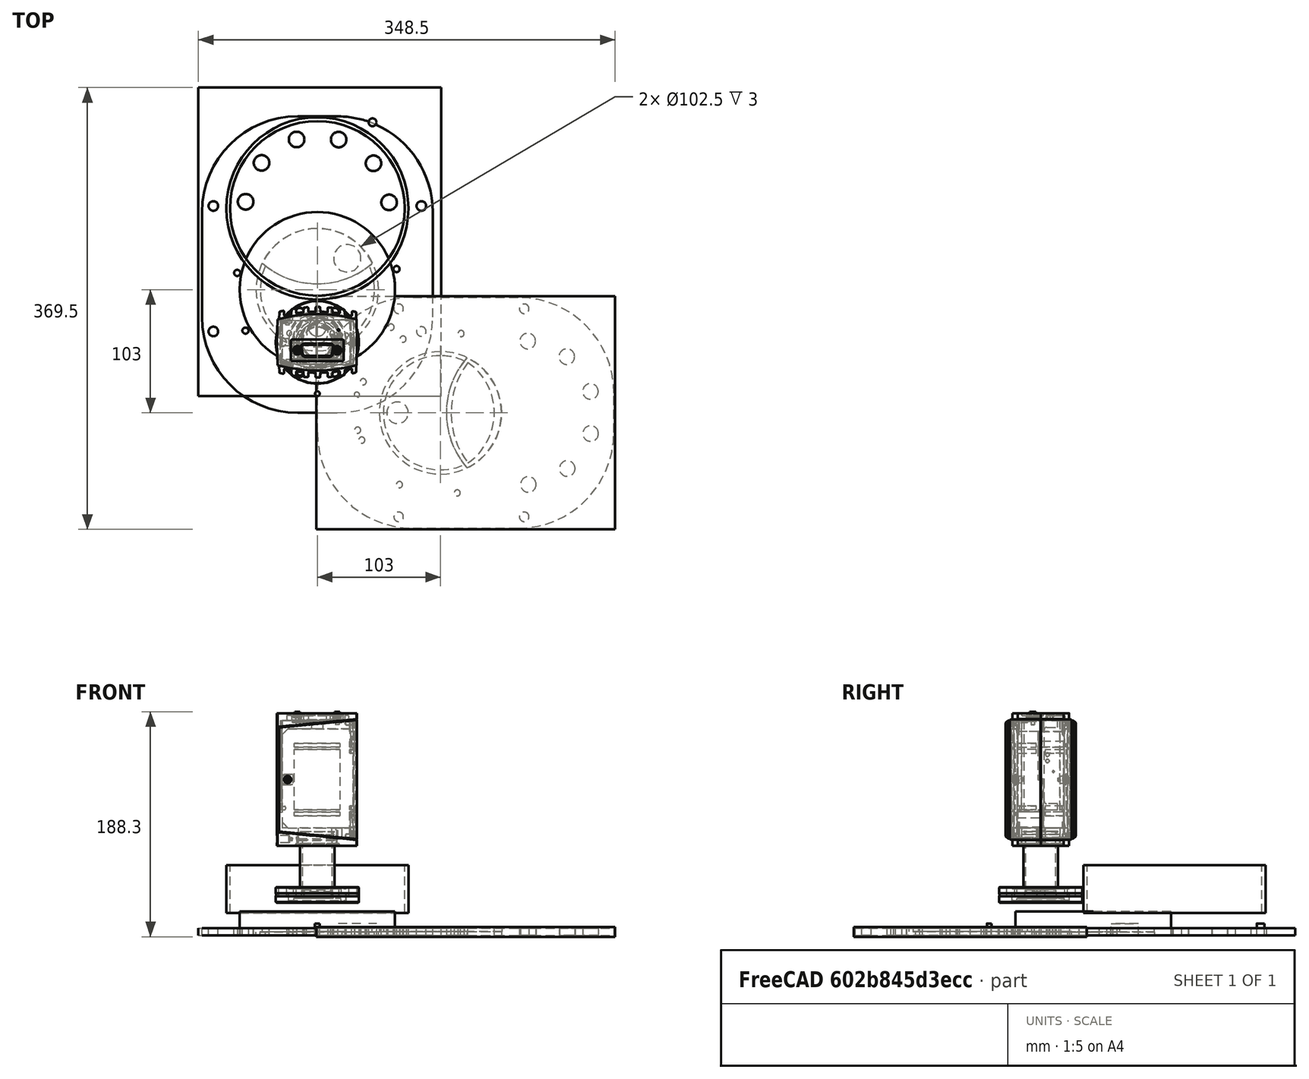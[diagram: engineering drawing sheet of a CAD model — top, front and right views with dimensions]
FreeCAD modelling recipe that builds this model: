
FCSTD DOCUMENT  (FreeCAD 0.18R16033 (Git))
Label: mk_3_5
License: All rights reserved
LicenseURL: http://en.wikipedia.org/wiki/All_rights_reserved
objects: Part::Cylinder×38, Part::FeaturePython×8, Path::FeaturePython×8, Part::Cut×7, Part::MultiFuse×6, Part::MultiCommon×4, Part::Box×3, Part::Fillet×2, App::FeaturePython×2, App::DocumentObjectGroup×2, Path::FeatureCompoundPython×2, Spreadsheet::Sheet×1, Part::Feature×1
note: 72 computed .brp shape members not serialized (recipe doc carries the construction recipe); baked Part::Feature solids carry a one-line shape summary decoded from their .brp

FEATURE [Part::Box] Box  label="Cube"
  AttacherType = Attacher::AttachEngine3D
  Height = 6.2
  Length = 193
  Placement = pos=(-96.5,0,0) rot=(0,0,1;0rad)
  Width = 248
FEATURE [Part::Cylinder] Cylinder004  label="Chamber001"
  Angle = 360
  AttacherType = Attacher::AttachEngine3D
  Height = 20
  Placement = pos=(0,149,0) rot=(0,0,1;0rad)
  Radius = 70.0875
  expr: Placement.Base.x = 0
  expr: Radius = 5.5625 * 25.2 / 2
FEATURE [Part::Cylinder] Cylinder005
  Angle = 360
  AttacherType = Attacher::AttachEngine3D
  Height = 20
  Placement = pos=(0,74,0) rot=(0,0,1;0rad)
  Radius = 51
  expr: Placement.Base.x = 0
  expr: Radius = 102 / 2
FEATURE [Part::MultiCommon] Common  label="Inlet"
  Placement = pos=(0,29,0) rot=(0,0,1;0rad)
  Shapes = -> [Cylinder004,Cylinder005]
FEATURE [Part::Cylinder] Cylinder012  label="Threaded"
  Angle = 360
  AttacherType = Attacher::AttachEngine3D
  Height = 19.5
  Placement = pos=(36.025,58.5,-4) rot=(0,0,1;0rad)
  Radius = 2.57969
  expr: Placement.Base.x = 105 - 68.675 - 0.3
  expr: Radius = 13 / 64 * 25.4 / 2
FEATURE [Part::FeaturePython] Array  label="TurboMounts"  # Draft array (typed FeaturePython)
  Angle = 208
  ArrayType = 1
  Axis = (0,0,1)
  Base = -> Cylinder012
  Center = (0,0,0)
  Fuse = false
  IntervalAxis = (0,0,0)
  IntervalX = (1,0,0)
  IntervalY = (0,1,0)
  IntervalZ = (0,0,0)
  NumberPolar = 6
  NumberX = 2
  NumberY = 2
  NumberZ = 1
  Placement = pos=(0,102,0) rot=(0,0,1;1.90241rad)
FEATURE [Part::Cylinder] Cylinder051  label="Flange001"
  Angle = 360
  AttacherType = Attacher::AttachEngine3D
  Height = 3
  Placement = pos=(0,68,0) rot=(0,0,1;0rad)
  Radius = 51.25
  expr: Radius = 102.5 / 2
FEATURE [Part::Cylinder] Cylinder052  label="Flange002"
  Angle = 360
  AttacherType = Attacher::AttachEngine3D
  Height = 3
  Placement = pos=(0,68,0) rot=(0,0,1;0rad)
  Radius = 47.75
  expr: Radius = 51.25 - 3.5
FEATURE [Part::Cut] Cut001  label="CenteringRingGroove"
  Base = -> Cylinder051
  Placement = pos=(0,35,0) rot=(0,0,1;0rad)
  Tool = -> Cylinder052
FEATURE [Part::Cylinder] Cylinder002  label="ChamberWall"
  Angle = 360
  AttacherType = Attacher::AttachEngine3D
  Height = 40
  Placement = pos=(0,148,0) rot=(0,0,1;0rad)
  Radius = 76.2
  expr: Radius = 3 * 25.4
FEATURE [Part::Cylinder] Cylinder008  label="ChamberWall001"
  Angle = 360
  AttacherType = Attacher::AttachEngine3D
  Height = 40
  Placement = pos=(0,148,0) rot=(0,0,1;0rad)
  Radius = 73.025
  expr: Radius = (3 - 0.125) * 25.4
FEATURE [Part::Cut] Cut  label="ChamberWall002"
  Base = -> Cylinder002
  Placement = pos=(0,23,19) rot=(0,0,1;0rad)
  Tool = -> Cylinder008
FEATURE [Spreadsheet::Sheet] Spreadsheet  label="Sizes"
  cells = A1=Baseplate width; B1(BASE_WIDTH)=195; A2=Baseplate length; B2(BASE_LENGTH)=255
FEATURE [Part::Cylinder] Cylinder
  Angle = 360
  AttacherType = Attacher::AttachEngine3D
  Height = 10
  Placement = pos=(25,129.26,0) rot=(0,0,1;0rad)
  Radius = 11.4
  expr: Placement.Base.y = 117.86 + 11.4
  expr: Radius = 22.8 / 2
FEATURE [Part::Cylinder] Cylinder053  label="Flange"
  Angle = 360
  AttacherType = Attacher::AttachEngine3D
  Height = 20
  Placement = pos=(0,103,0) rot=(0,0,1;0rad)
  Radius = 65
  expr: Placement.Base.x = 0
  expr: Radius = 130 / 2
FEATURE [Part::Cylinder] Cylinder054  label="Cylinder006"
  Angle = 360
  AttacherType = Attacher::AttachEngine3D
  Height = 10
  Placement = pos=(46.19,243,0) rot=(0,0,1;0rad)
  Radius = 3.275
  expr: Radius = 6.55 / 2
FEATURE [Part::Feature] Part__Feature002  label="353-502"
  Placement = pos=(0,59,75) rot=(1,0,0;1.5708rad)
  shape: bbox 69.52 x 69.52 x 159.7 mm, 770 faces, 3 solids (baked)
FEATURE [Part::Cylinder] Cylinder157  label="Gland1"
  Angle = 360
  AttacherType = Attacher::AttachEngine3D
  Height = 3.175
  Radius = 24
FEATURE [Part::Cylinder] Cylinder158  label="Cylinder010"
  Angle = 360
  AttacherType = Attacher::AttachEngine3D
  Height = 41.275
  Radius = 20.635
  expr: Radius = (25.4 + 15.87) / 2
  expr: Height = 25.4 + 15.875
FEATURE [Part::Cut] Cut020
  Base = -> Cylinder157
  Placement = pos=(0,61,0) rot=(0,0,1;0rad)
  Tool = -> Cylinder158
FEATURE [Part::Cylinder] Cylinder159  label="Cylinder011"
  Angle = 360
  AttacherType = Attacher::AttachEngine3D
  Height = 21
  Placement = pos=(0,67,-4) rot=(0,0,1;0rad)
  Radius = 9
  expr: Placement.Base.x = 0
FEATURE [Part::Cylinder] Cylinder163  label="Cylinder015"
  Angle = 360
  AttacherType = Attacher::AttachEngine3D
  Height = 29
  Placement = pos=(-14.5,33.7,-7) rot=(0,0,1;0rad)
  Radius = 2.58
FEATURE [Part::Cylinder] Cylinder164  label="Cylinder016"
  Angle = 360
  AttacherType = Attacher::AttachEngine3D
  Height = 29
  Placement = pos=(15,33,-9) rot=(0,0,1;0rad)
  Radius = 2.28
FEATURE [Part::Cylinder] Cylinder165  label="Cylinder017"
  Angle = 360
  AttacherType = Attacher::AttachEngine3D
  Height = 10
  Placement = pos=(-87,173,0) rot=(0,0,1;0rad)
  Radius = 4
  expr: Radius = 4
FEATURE [Part::Cylinder] Cylinder166  label="Cylinder018"
  Angle = 360
  AttacherType = Attacher::AttachEngine3D
  Height = 10
  Placement = pos=(87,68,0) rot=(0,0,1;0rad)
  Radius = 4
  expr: Radius = 4
FEATURE [Part::Cylinder] Cylinder167  label="Cylinder019"
  Angle = 360
  AttacherType = Attacher::AttachEngine3D
  Height = 10
  Placement = pos=(-87,68,0) rot=(0,0,1;0rad)
  Radius = 4
  expr: Radius = 4
FEATURE [Part::Cylinder] Cylinder168  label="Cylinder020"
  Angle = 360
  AttacherType = Attacher::AttachEngine3D
  Height = 10
  Placement = pos=(87,173,0) rot=(0,0,1;0rad)
  Radius = 4
  expr: Radius = 4
FEATURE [Part::Box] Box001  label="Cube001"
  AttacherType = Attacher::AttachEngine3D
  Height = 6.2
  Length = 203
  Placement = pos=(-99.5,14,0) rot=(0,0,1;0rad)
  Width = 258
FEATURE [Part::Cylinder] Cylinder169  label="Cylinder021"
  Angle = 360
  AttacherType = Attacher::AttachEngine3D
  Height = 10
  Placement = pos=(0,16,0) rot=(0,0,1;0rad)
  Radius = 2
FEATURE [Part::Cylinder] Cylinder170  label="Cylinder022"
  Angle = 360
  AttacherType = Attacher::AttachEngine3D
  Height = 10
  Placement = pos=(60,181,0) rot=(0,0,1;0rad)
  Radius = 6.5
  expr: Radius = 13 / 2
FEATURE [Part::FeaturePython] Array001  # Draft array (typed FeaturePython)
  Angle = 170
  ArrayType = 1
  Axis = (0,0,1)
  Base = -> Cylinder170
  Center = (0,176,0)
  Fuse = false
  IntervalAxis = (0,0,0)
  IntervalX = (1,0,0)
  IntervalY = (0,1,0)
  IntervalZ = (0,0,0)
  NumberPolar = 6
  NumberX = 2
  NumberY = 2
  NumberZ = 1
  Placement = pos=(0,-5,0) rot=(0,0,1;0rad)
  expr: Center.y = 148 + 28
FEATURE [Part::Fillet] Fillet
  Base = -> Box
  Edges = 4 edges r=80: [Edge1,Edge3,Edge5,Edge7]
FEATURE [Part::MultiFuse] Fusion
  Shapes = -> [Common,Array,Cut001,Cylinder164,Cylinder163,Cylinder159,Cylinder165,Cylinder166,Cylinder167,Cylinder168]
FEATURE [Part::MultiFuse] Fusion001
  Shapes = -> [Fusion,Array001]
FEATURE [Part::Cut] Cut021
  Base = -> Fillet
  Tool = -> Fusion001
FEATURE [Part::Cut] Cut022
  Base = -> Fillet
  Placement = pos=(0,0,6.2) rot=(0,1,0;3.14159rad)
  Tool = -> Fusion001
FEATURE [Part::Cylinder] Cylinder171
  Angle = 360
  AttacherType = Attacher::AttachEngine3D
  Height = 20
  Placement = pos=(0,68,0) rot=(0,0,1;0rad)
  Radius = 51
  expr: Placement.Base.x = 0
  expr: Radius = 102 / 2
FEATURE [Part::Cylinder] Cylinder172  label="Chamber002"
  Angle = 360
  AttacherType = Attacher::AttachEngine3D
  Height = 6.2
  Placement = pos=(0,153,0) rot=(0,0,1;0rad)
  Radius = 70.0875
  expr: Placement.Base.x = 0
  expr: Radius = 5.5625 * 25.2 / 2
FEATURE [Part::MultiCommon] Common001  label="Inlet001"
  Placement = pos=(0,29,0) rot=(0,0,1;0rad)
  Shapes = -> [Cylinder172,Cylinder171]
FEATURE [Part::MultiFuse] Fusion002
  Placement = pos=(0,0,0) rot=(0,0,-1;1.5708rad)
  Shapes = -> [Common001,Cut022]
FEATURE [Part::Cylinder] Cylinder173  label="Chamber003"
  Angle = 360
  AttacherType = Attacher::AttachEngine3D
  Height = 6.2
  Placement = pos=(0,159,0) rot=(0,0,1;0rad)
  Radius = 70.0875
  expr: Placement.Base.x = 0
  expr: Radius = 5.5625 * 25.2 / 2
FEATURE [Part::Cylinder] Cylinder174
  Angle = 360
  AttacherType = Attacher::AttachEngine3D
  Height = 20
  Placement = pos=(0,63,0) rot=(0,0,1;0rad)
  Radius = 51
  expr: Placement.Base.x = 0
  expr: Radius = 102 / 2
FEATURE [Part::Cylinder] Cylinder175
  Angle = 360
  AttacherType = Attacher::AttachEngine3D
  Height = 10
  Placement = pos=(87,173,0) rot=(0,0,1;0rad)
  Radius = 4
  expr: Radius = 4
FEATURE [Part::Cylinder] Cylinder176  label="Chamber004"
  Angle = 360
  AttacherType = Attacher::AttachEngine3D
  Height = 20
  Placement = pos=(0,149,0) rot=(0,0,1;0rad)
  Radius = 70.0875
  expr: Placement.Base.x = 0
  expr: Radius = 5.5625 * 25.2 / 2
FEATURE [Part::Cylinder] Cylinder177  label="Cylinder176"
  Angle = 360
  AttacherType = Attacher::AttachEngine3D
  Height = 29
  Placement = pos=(15,33,-9) rot=(0,0,1;0rad)
  Radius = 2.28
FEATURE [Part::Cylinder] Cylinder178  label="Threaded001"
  Angle = 360
  AttacherType = Attacher::AttachEngine3D
  Height = 19.5
  Placement = pos=(36.025,58.5,-4) rot=(0,0,1;0rad)
  Radius = 2.57969
  expr: Placement.Base.x = 105 - 68.675 - 0.3
  expr: Radius = 13 / 64 * 25.4 / 2
FEATURE [Part::FeaturePython] Array002  label="TurboMounts001"  # Draft array (typed FeaturePython)
  Angle = 208
  ArrayType = 1
  Axis = (0,0,1)
  Base = -> Cylinder178
  Center = (0,0,0)
  Fuse = false
  IntervalAxis = (0,0,0)
  IntervalX = (1,0,0)
  IntervalY = (0,1,0)
  IntervalZ = (0,0,0)
  NumberPolar = 6
  NumberX = 2
  NumberY = 2
  NumberZ = 1
  Placement = pos=(0,102,0) rot=(0,0,1;1.90241rad)
FEATURE [Part::Cylinder] Cylinder179  label="Flange003"
  Angle = 360
  AttacherType = Attacher::AttachEngine3D
  Height = 3
  Placement = pos=(0,68,0) rot=(0,0,1;0rad)
  Radius = 51.25
  expr: Radius = 102.5 / 2
FEATURE [Part::Cylinder] Cylinder180  label="Cylinder177"
  Angle = 360
  AttacherType = Attacher::AttachEngine3D
  Height = 10
  Placement = pos=(60,181,0) rot=(0,0,1;0rad)
  Radius = 6.5
  expr: Radius = 13 / 2
FEATURE [Part::Cylinder] Cylinder181  label="Cylinder178"
  Angle = 360
  AttacherType = Attacher::AttachEngine3D
  Height = 29
  Placement = pos=(-14.5,33.7,-7) rot=(0,0,1;0rad)
  Radius = 2.58
FEATURE [Part::Cylinder] Cylinder182  label="Cylinder179"
  Angle = 360
  AttacherType = Attacher::AttachEngine3D
  Height = 10
  Placement = pos=(-87,173,0) rot=(0,0,1;0rad)
  Radius = 4
  expr: Radius = 4
FEATURE [Part::Cylinder] Cylinder183  label="Cylinder180"
  Angle = 360
  AttacherType = Attacher::AttachEngine3D
  Height = 21
  Placement = pos=(0,67,-4) rot=(0,0,1;0rad)
  Radius = 9
  expr: Placement.Base.x = 0
FEATURE [Part::Cylinder] Cylinder184  label="Cylinder181"
  Angle = 360
  AttacherType = Attacher::AttachEngine3D
  Height = 10
  Placement = pos=(87,68,0) rot=(0,0,1;0rad)
  Radius = 4
  expr: Radius = 4
FEATURE [Part::Cylinder] Cylinder185  label="Flange004"
  Angle = 360
  AttacherType = Attacher::AttachEngine3D
  Height = 3
  Placement = pos=(0,68,0) rot=(0,0,1;0rad)
  Radius = 47.75
  expr: Radius = 51.25 - 3.5
FEATURE [Part::Cut] Cut023  label="CenteringRingGroove001"
  Base = -> Cylinder179
  Placement = pos=(0,35,0) rot=(0,0,1;0rad)
  Tool = -> Cylinder185
FEATURE [Part::FeaturePython] Array003  # Draft array (typed FeaturePython)
  Angle = 170
  ArrayType = 1
  Axis = (0,0,1)
  Base = -> Cylinder180
  Center = (0,176,0)
  Fuse = false
  IntervalAxis = (0,0,0)
  IntervalX = (1,0,0)
  IntervalY = (0,1,0)
  IntervalZ = (0,0,0)
  NumberPolar = 6
  NumberX = 2
  NumberY = 2
  NumberZ = 1
  Placement = pos=(0,-5,0) rot=(0,0,1;0rad)
  expr: Center.y = 148 + 28
FEATURE [Part::Cylinder] Cylinder186
  Angle = 360
  AttacherType = Attacher::AttachEngine3D
  Height = 20
  Placement = pos=(0,74,0) rot=(0,0,1;0rad)
  Radius = 51
  expr: Placement.Base.x = 0
  expr: Radius = 102 / 2
FEATURE [Part::MultiCommon] Common002  label="Inlet002"
  Placement = pos=(0,29,0) rot=(0,0,1;0rad)
  Shapes = -> [Cylinder176,Cylinder186]
FEATURE [Part::Cylinder] Cylinder187
  Angle = 360
  AttacherType = Attacher::AttachEngine3D
  Height = 10
  Placement = pos=(-87,68,0) rot=(0,0,1;0rad)
  Radius = 4
  expr: Radius = 4
FEATURE [Part::MultiFuse] Fusion005
  Shapes = -> [Common002,Array002,Cut023,Cylinder177,Cylinder181,Cylinder183,Cylinder182,Cylinder184,Cylinder187,Cylinder175]
FEATURE [Part::MultiFuse] Fusion004
  Shapes = -> [Fusion005,Array003]
FEATURE [Part::Box] Box002  label="Cube002"
  AttacherType = Attacher::AttachEngine3D
  Height = 6.2
  Length = 193
  Placement = pos=(-96.5,0,0) rot=(0,0,1;0rad)
  Width = 248
FEATURE [Part::Fillet] Fillet001
  Base = -> Box002
  Edges = 4 edges r=80: [Edge1,Edge3,Edge5,Edge7]
FEATURE [Part::MultiCommon] Common003  label="Inlet003"
  Placement = pos=(0,29,0) rot=(0,0,1;0rad)
  Shapes = -> [Cylinder173,Cylinder174]
FEATURE [Part::Cut] Cut024
  Base = -> Fillet001
  Placement = pos=(0,0,6.2) rot=(0,1,0;3.14159rad)
  Tool = -> Fusion004
FEATURE [Part::MultiFuse] Fusion003
  Placement = pos=(0,0,0) rot=(0,0,-1;1.5708rad)
  Shapes = -> [Common003,Cut024]
FEATURE [App::FeaturePython] SetupSheet  # Path/CAM operation (typed FeaturePython)
  ClearanceHeightExpression = OpStockZMax+SetupSheet.ClearanceHeightOffset
  ClearanceHeightOffset = 5
  FinalDepthExpression = OpFinalDepth
  HorizRapid = 0
  SafeHeightExpression = OpStockZMax+SetupSheet.SafeHeightOffset
  SafeHeightOffset = 3
  StartDepthExpression = OpStartDepth
  StepDownExpression = OpToolDiameter
  VertRapid = 0
FEATURE [Part::FeaturePython] Clone  label="Model-Fusion003"  # Draft clone (typed FeaturePython)
  AttacherType = Attacher::AttachEngine3D
  Fuse = false
  Objects = -> [Fusion003]
  PathResource = Model
  Placement = pos=(0,0,0) rot=(0,0,-1;1.5708rad)
  Scale = (1,1,1)
FEATURE [App::DocumentObjectGroup] Model
  Group = -> [Clone]
FEATURE [Part::FeaturePython] Stock001  # WARN: FeaturePython — macro-defined, semantics opaque (R4)
  Base = -> Model
  ExtXneg = 1
  ExtXpos = 1
  ExtYneg = 1
  ExtYpos = 1
  ExtZneg = 1
  ExtZpos = 1
  Placement = pos=(-1.77e-14,-96.5,-9e-16) rot=(0,0,1;0rad)
  StockType = FromBase
FEATURE [Path::FeaturePython] T2__250_End_Mill  label="T2: 250 End Mill"  # Path/CAM operation (typed FeaturePython)
  HorizFeed = 11
  HorizRapid = 0
  SpindleDir = 0
  SpindleSpeed = 13000
  ToolNumber = 1
  VertFeed = 1
  VertRapid = 0
  expr: HorizRapid = SetupSheet.HorizRapid
  expr: VertRapid = SetupSheet.VertRapid
FEATURE [Path::FeaturePython] Contour  # Path/CAM operation (typed FeaturePython)
  Active = false
  AreaParams:
    OpenMode = 0
    Angle = 45.0
    MinArcPoints = 4
    Coplanar = 2
    Tolerance = 1e-07
    CleanDistance = 0.0
    PocketExtraOffset = 0.0
    RoundPrecision = 0.0
    AngleShift = 0.0
    SubjectFill = 0
    PocketMode = 0
    PocketLastStepover = 0.0
    Simplify = False
    SectionTolerance = 1e-06
    MaxArcPoints = 100
    Offset = 3.175
    Accuracy = 0.01
    LastStepover = 0.0
    PocketStepover = 0.0
    ClipFill = 0
    ToolRadius = 1.0
    Outline = False
    ClipperScale = 10000000.0
    FromCenter = False
    Explode = False
    EndType = 0
    Shift = 0.0
    ExtraPass = 0
    Project = False
    JoinType = 0
    Thicken = False
    Stepdown = 1.0
    SectionMode = 2
    MiterLimit = 2.0
    Deflection = 0.01
    Reorient = True
    FitArcs = True
    SectionCount = -1
    SectionOffset = 0.0
    Stepover = 0.0
    Unit = 1.0
    Fill = 0
  ClearanceHeight = 12.2
  Direction = 0
  FinalDepth = -2
  JoinType = 0
  MiterLimit = 0.1
  OffsetExtra = 0
  OpFinalDepth = -1
  OpStartDepth = 7.2
  OpStockZMax = 7.2
  OpStockZMin = -1
  OpToolDiameter = 6.35
  PathParams = {'resume_height': 5.0, 'feedrate': 11.0, 'verbose': True, 'orientation': 1, 'return_end': True, 'preamble': False, 'retraction': 12.2, 'feedrate_v': 1.0}
  SafeHeight = 5
  Side = 0
  StartDepth = 7.2
  StartPoint = (0,0,0)
  StepDown = 1
  ToolController = -> T2__250_End_Mill
  UseComp = true
  UseStartPoint = false
  expr: ClearanceHeight = OpStockZMax + SetupSheet.ClearanceHeightOffset
  expr: SafeHeight = 5
  expr: StepDown = 1
  expr: FinalDepth = -2
  expr: StartDepth = OpStartDepth
FEATURE [Path::FeaturePython] Pocket_Shape  # Path/CAM operation (typed FeaturePython)
  Active = true
  AreaParams:
    OpenMode = 0
    Angle = 45.0
    MinArcPoints = 4
    Coplanar = 0
    Tolerance = 1e-07
    CleanDistance = 0.0
    PocketExtraOffset = 0.0
    RoundPrecision = 0.0
    AngleShift = 0.0
    SubjectFill = 0
    PocketMode = 3
    PocketLastStepover = 0.0
    Simplify = False
    SectionTolerance = 1e-06
    MaxArcPoints = 100
    Offset = 0.0
    Accuracy = 0.01
    LastStepover = 0.0
    PocketStepover = 6.35
    ClipFill = 0
    ToolRadius = 3.175
    Outline = False
    ClipperScale = 10000000.0
    FromCenter = True
    Explode = False
    EndType = 0
    Shift = 0.0
    ExtraPass = 0
    Project = False
    JoinType = 0
    Thicken = False
    Stepdown = 1.0
    SectionMode = 2
    MiterLimit = 2.0
    Deflection = 0.01
    Reorient = True
    FitArcs = True
    SectionCount = -1
    SectionOffset = 0.0
    Stepover = 0.0
    Unit = 1.0
    Fill = 0
  Base = -> [Clone]
  ClearanceHeight = 12.2
  CutMode = 0
  ExtraOffset = 0
  FinalDepth = -2
  FinishDepth = 0
  KeepToolDown = false
  MinTravel = false
  OffsetPattern = 2
  OpFinalDepth = 0
  OpStartDepth = 7.2
  OpStockZMax = 7.2
  OpStockZMin = -1
  OpToolDiameter = 6.35
  PathParams = {'resume_height': 10.2, 'feedrate': 11.0, 'verbose': True, 'orientation': 1, 'return_end': True, 'preamble': False, 'retraction': 12.2, 'feedrate_v': 1.0}
  SafeHeight = 10.2
  StartAt = 0
  StartDepth = 7.2
  StartPoint = (0,0,0)
  StepDown = 1
  StepOver = 100
  ToolController = -> T2__250_End_Mill
  UseOutline = false
  UseStartPoint = false
  ZigZagAngle = 45
  expr: ClearanceHeight = OpStockZMax + SetupSheet.ClearanceHeightOffset
  expr: SafeHeight = OpStockZMax + SetupSheet.SafeHeightOffset
  expr: StepDown = 1
  expr: FinalDepth = -2
  expr: StartDepth = OpStartDepth
FEATURE [Path::FeatureCompoundPython] Operations  # Path/CAM operation (typed FeaturePython)
  Group = -> [Contour,Pocket_Shape]
  UsePlacements = false
FEATURE [Path::FeaturePython] Job  # Path/CAM operation (typed FeaturePython)
  GeometryTolerance = 0.01
  Model = -> Model
  Operations = -> Operations
  PostProcessor = 7
  PostProcessorOutputFile = <userpath>/NAS/primary_a/Projects/ion_printer/files/ionprinter/mechanical/GCode/mk3_5_plate/mk3_5_250_contour.ngc
  SetupSheet = -> SetupSheet
  Stock = -> Stock001
  ToolController = -> [T2__250_End_Mill]
FEATURE [App::FeaturePython] SetupSheet001  # Path/CAM operation (typed FeaturePython)
  ClearanceHeightExpression = OpStockZMax+SetupSheet001.ClearanceHeightOffset
  ClearanceHeightOffset = 5
  FinalDepthExpression = OpFinalDepth
  HorizRapid = 0
  SafeHeightExpression = OpStockZMax+SetupSheet001.SafeHeightOffset
  SafeHeightOffset = 3
  StartDepthExpression = OpStartDepth
  StepDownExpression = OpToolDiameter
  VertRapid = 0
FEATURE [Part::FeaturePython] Clone001  label="Model-Fusion004"  # Draft clone (typed FeaturePython)
  AttacherType = Attacher::AttachEngine3D
  Fuse = false
  Objects = -> [Fusion003]
  PathResource = Model
  Placement = pos=(0,0,0) rot=(0,0,-1;1.5708rad)
  Scale = (1,1,1)
FEATURE [App::DocumentObjectGroup] Model001
  Group = -> [Clone001]
FEATURE [Part::FeaturePython] Stock002  # WARN: FeaturePython — macro-defined, semantics opaque (R4)
  Base = -> Model001
  ExtXneg = 1
  ExtXpos = 1
  ExtYneg = 1
  ExtYpos = 1
  ExtZneg = 1
  ExtZpos = 1
  Placement = pos=(-1.77e-14,-96.5,-9e-16) rot=(0,0,1;0rad)
  StockType = FromBase
FEATURE [Path::FeaturePython] T1__125_End_Mill  label="T1: 125 End Mill"  # Path/CAM operation (typed FeaturePython)
  HorizFeed = 7
  HorizRapid = 0
  SpindleDir = 0
  SpindleSpeed = 13000
  ToolNumber = 1
  VertFeed = 1
  VertRapid = 0
  expr: HorizRapid = SetupSheet001.HorizRapid
  expr: VertRapid = SetupSheet001.VertRapid
FEATURE [Path::FeaturePython] Pocket_Shape001  # Path/CAM operation (typed FeaturePython)
  Active = false
  AreaParams:
    OpenMode = 0
    Angle = 45.0
    MinArcPoints = 4
    Coplanar = 0
    Tolerance = 1e-07
    CleanDistance = 0.0
    PocketExtraOffset = 0.0
    RoundPrecision = 0.0
    AngleShift = 0.0
    SubjectFill = 0
    PocketMode = 3
    PocketLastStepover = 0.0
    Simplify = False
    SectionTolerance = 1e-06
    MaxArcPoints = 100
    Offset = 0.0
    Accuracy = 0.01
    LastStepover = 0.0
    PocketStepover = 3.17
    ClipFill = 0
    ToolRadius = 1.585
    Outline = False
    ClipperScale = 10000000.0
    FromCenter = True
    Explode = False
    EndType = 0
    Shift = 0.0
    ExtraPass = 0
    Project = False
    JoinType = 0
    Thicken = False
    Stepdown = 1.0
    SectionMode = 2
    MiterLimit = 2.0
    Deflection = 0.01
    Reorient = True
    FitArcs = True
    SectionCount = -1
    SectionOffset = 0.0
    Stepover = 0.0
    Unit = 1.0
    Fill = 0
  Base = -> [Clone001]
  ClearanceHeight = 12.2
  CutMode = 1
  ExtraOffset = 0
  FinalDepth = 3.2
  FinishDepth = 0
  KeepToolDown = false
  MinTravel = false
  OffsetPattern = 2
  OpFinalDepth = 3.2
  OpStartDepth = 7.2
  OpStockZMax = 7.2
  OpStockZMin = -1
  OpToolDiameter = 3.17
  PathParams = {'resume_height': 10.2, 'feedrate': 7.0, 'verbose': True, 'orientation': 0, 'return_end': True, 'preamble': False, 'retraction': 12.2, 'feedrate_v': 1.0}
  SafeHeight = 10.2
  StartAt = 0
  StartDepth = 7.2
  StartPoint = (0,0,0)
  StepDown = 1
  StepOver = 100
  ToolController = -> T1__125_End_Mill
  UseOutline = false
  UseStartPoint = false
  ZigZagAngle = 45
  expr: ClearanceHeight = OpStockZMax + SetupSheet001.ClearanceHeightOffset
  expr: SafeHeight = OpStockZMax + SetupSheet001.SafeHeightOffset
  expr: StepDown = 1
  expr: FinalDepth = OpFinalDepth
  expr: StartDepth = OpStartDepth
FEATURE [Path::FeaturePython] Drilling  # Path/CAM operation (typed FeaturePython)
  Active = true
  AddTipLength = false
  Base = -> [Clone001]
  ClearanceHeight = 12.2
  DwellEnabled = false
  DwellTime = 0
  FinalDepth = 5.5
  OpFinalDepth = 9e-16
  OpStartDepth = 7.2
  OpStockZMax = 7.2
  OpStockZMin = -1
  OpToolDiameter = 3.17
  PeckDepth = 0
  PeckEnabled = false
  RetractHeight = 10
  ReturnLevel = 0
  SafeHeight = 10.2
  StartDepth = 7.2
  ToolController = -> T1__125_End_Mill
  expr: ClearanceHeight = OpStockZMax + SetupSheet001.ClearanceHeightOffset
  expr: SafeHeight = OpStockZMax + SetupSheet001.SafeHeightOffset
  expr: FinalDepth = 5.5
  expr: StartDepth = OpStartDepth
FEATURE [Path::FeatureCompoundPython] Operations001  # Path/CAM operation (typed FeaturePython)
  Group = -> [Pocket_Shape001,Drilling]
  UsePlacements = false
FEATURE [Path::FeaturePython] Job001  # Path/CAM operation (typed FeaturePython)
  GeometryTolerance = 0.01
  Model = -> Model001
  Operations = -> Operations001
  PostProcessor = 7
  PostProcessorOutputFile = <userpath>/NAS/primary_a/Projects/ion_printer/files/ionprinter/mechanical/GCode/mk3_5_plate/mk3_5_125.ngc
  SetupSheet = -> SetupSheet001
  Stock = -> Stock002
  ToolController = -> [T1__125_End_Mill]
